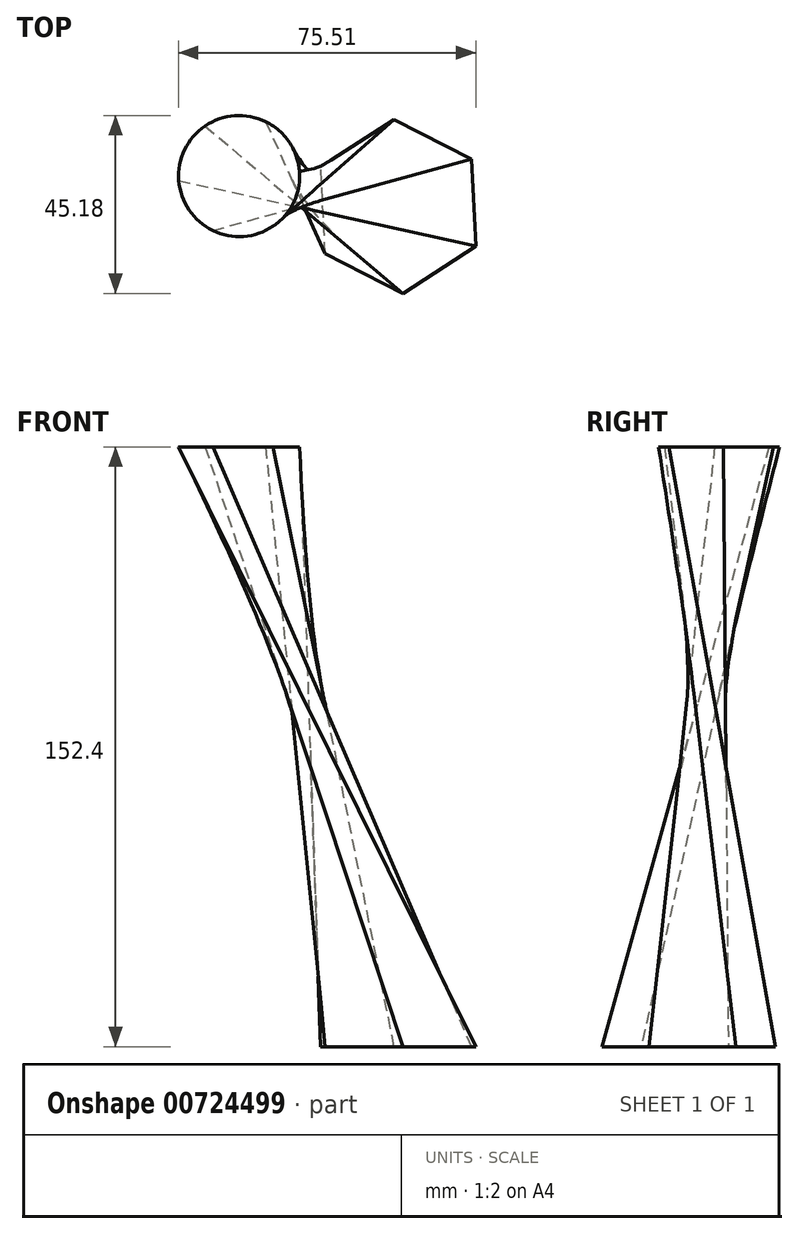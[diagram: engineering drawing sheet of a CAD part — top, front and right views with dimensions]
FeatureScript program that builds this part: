
annotation { "Feature Type Name" : "Feature", "Feature Type Description" : "" }
export const myFeature = defineFeature(function(context is Context, id is Id, definition is map)
    precondition{}
    {
        {
            var Q0;
            Q0=qCreatedBy(makeId("Top.planeOp"),FACE);
            cPlane(context, id + "F0", {"entities" : qUnion([Q0]), "cplaneType" : CPlaneType.OFFSET, "offset" : 152.4 * mm, "width" : 152.4 * mm, "height" : 152.4 * mm});
        }
        {
            var Q0;
            Q0=qCreatedBy(id+"F0.planeOp",FACE);
            var sketch = newSketch(context, id + "F1", { "sketchPlane" : qUnion([Q0])});
            skCircle(sketch, "E0", {"center": v(-40.42, 29.3) * mm, "radius": 15.39 * mm});
            skSolve(sketch);
        }
        {
            var Q0;
            Q0=qCreatedBy(makeId("Top.planeOp"),FACE);
            var sketch = newSketch(context, id + "F2", { "sketchPlane" : qUnion([Q0])});
            skCircle(sketch, "E1.cCircle", {"center": v(0, 21.59) * mm, "radius": 22.12 * mm, "construction": true});
            skLineSegment(sketch, "E1.0", {"start": v(18.55, 33.62) * mm, "end": v(19.7, 11.54) * mm});
            skLineSegment(sketch, "E1.1", {"start": v(19.7, 11.54) * mm, "end": v(1.15, -0.5) * mm});
            skLineSegment(sketch, "E1.2", {"start": v(1.15, -0.5) * mm, "end": v(-18.55, 9.55) * mm});
            skLineSegment(sketch, "E1.3", {"start": v(-18.55, 9.55) * mm, "end": v(-19.7, 31.63) * mm});
            skLineSegment(sketch, "E1.4", {"start": v(-19.7, 31.63) * mm, "end": v(-1.15, 43.67) * mm});
            skLineSegment(sketch, "E1.5", {"start": v(-1.15, 43.67) * mm, "end": v(18.55, 33.62) * mm});
            skSolve(sketch);
        }
        {
            var Q0;
            Q0=makeQuery(id+"F1.imprint","IMPRINT",FACE,{"disambiguationData":[TD([[makeQuery(id+"F1.imprint","IMPRINT",EDGE,{"derivedFrom":sQuery(id+"F1.wireOp",EDGE,"E0")}),1.0]])]});
            var Q1;
            Q1=makeQuery(id+"F2.imprint","IMPRINT",FACE,{"disambiguationData":[TD([[makeQuery(id+"F2.imprint","IMPRINT",EDGE,{"derivedFrom":sQuery(id+"F2.wireOp",EDGE,"E1.0")}),-1.0]])]});
            loft(context, id + "F3", {"sheetProfilesArray" : [{ "sheetProfileEntities" : qUnion([Q0]) }, { "sheetProfileEntities" : qUnion([Q1]) }]});
        }
    });
